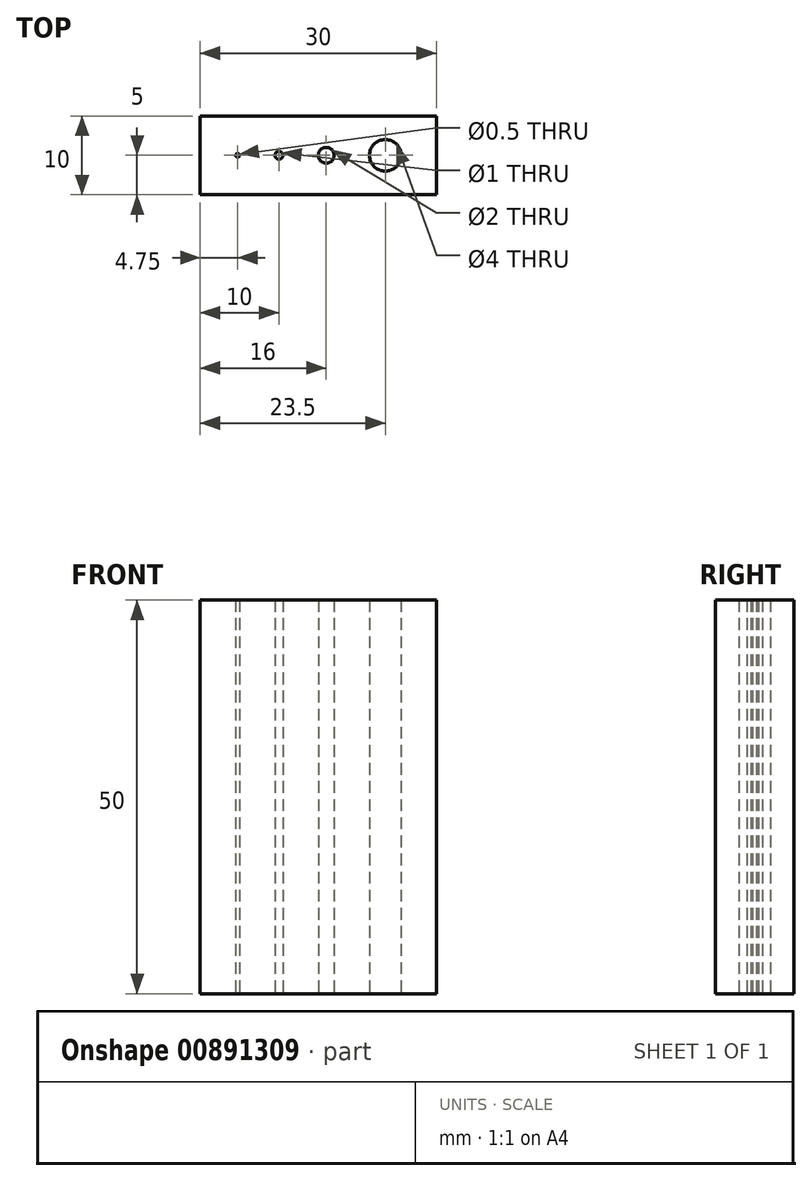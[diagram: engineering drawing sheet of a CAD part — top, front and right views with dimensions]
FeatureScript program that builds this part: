
annotation { "Feature Type Name" : "Feature", "Feature Type Description" : "" }
export const myFeature = defineFeature(function(context is Context, id is Id, definition is map)
    precondition{}
    {
        {
            var Q0;
            Q0=qCreatedBy(makeId("Top.planeOp"),FACE);
            var sketch = newSketch(context, id + "F0", { "sketchPlane" : qUnion([Q0])});
            skLineSegment(sketch, "E0.bottom", {"start": v(-15, 5) * mm, "end": v(15, 5) * mm});
            skLineSegment(sketch, "E0.top", {"start": v(-15, -5) * mm, "end": v(15, -5) * mm});
            skLineSegment(sketch, "E0.left", {"start": v(-15, 5) * mm, "end": v(-15, -5) * mm});
            skLineSegment(sketch, "E0.right", {"start": v(15, 5) * mm, "end": v(15, -5) * mm});
            skCircle(sketch, "E1", {"center": v(-10.25, 0) * mm, "radius": 0.25 * mm});
            skCircle(sketch, "E2", {"center": v(-5, 0) * mm, "radius": 0.5 * mm});
            skCircle(sketch, "E3", {"center": v(1, 0) * mm, "radius": 1 * mm});
            skCircle(sketch, "E4", {"center": v(8.5, 0) * mm, "radius": 2 * mm});
            skSolve(sketch);
        }
        {
            var Q0;
            Q0=makeQuery(id+"F0.imprint","IMPRINT",FACE,{"disambiguationData":[TD([[makeQuery(id+"F0.imprint","IMPRINT",EDGE,{"derivedFrom":sQuery(id+"F0.wireOp",EDGE,"E0.bottom")}),-1.0]])]});
            extrude(context, id + "F1", {"entities" : qUnion([Q0]), "depth" : 50 * mm, "offsetDistance" : 25 * mm});
        }
    });
